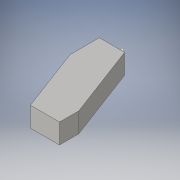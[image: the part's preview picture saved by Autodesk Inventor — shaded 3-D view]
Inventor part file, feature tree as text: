
AUTODESK INVENTOR PART (.ipt)
format: ipt  version: 2016 (Build 200138000, 138)  size: 2,810,368 bytes
history: native  units: in
note: dims shown in document units (in); Inventor stores cm internally (conversion verified against a paired STEP export)
features: sketch x5, extrude x4, other x3, projected_geometry x2
ambient origin geometry x8: Origin, YZ Plane, XZ Plane, XY Plane, X Axis, Y Axis, Z Axis, Center Point
bodies: Solid1 (feature_tree)
feature tree (14):
  other  "Finger Mold 2.iam"
  other  "Finger Mold.ipt:2"
  other  "Full Rubber Finger.ipt:1"
  extrude  "Extrusion2"  Depth=0.3937in TaperAngle=0.0deg
  extrude  "Extrusion3"  Depth=0.75in
  extrude  "Extrusion4"  Depth=0.87in
  extrude  "Extrusion5"  Depth=1.0in TaperAngle=0.0deg
  sketch  "Sketch74"
  sketch  "Sketch3"  dims[d0=0.3937in d4=0.9375in d5=0.0in]
  projected_geometry  "Projected Loop1"
  sketch  "Sketch4"  dims[d6=1.0in d7=0.0in d8=0.75in]
  projected_geometry  "Projected Loop2"
  sketch  "Sketch5"  dims[d9=0.57in d10=0.87in]
  sketch  "Sketch6"  dims[d11=1.0in d12=0.0in d13=1.0in d14=0.0in]
